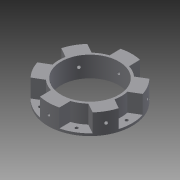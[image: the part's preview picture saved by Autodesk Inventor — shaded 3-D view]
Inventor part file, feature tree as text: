
AUTODESK INVENTOR PART (.ipt)
format: ipt  version: 2015 (Build 190159000, 159)  size: 173,056 bytes
history: native  units: in
note: dims shown in document units (in); Inventor stores cm internally (conversion verified against a paired STEP export)
features: sketch x5, extrude x3, hole x2, pattern_circular x2, plane x1
ambient origin geometry x8: Origin, YZ Plane, XZ Plane, XY Plane, X Axis, Y Axis, Z Axis, Center Point
bodies: Solid1 (feature_tree)
feature tree (13):
  extrude  "Extrusion1"  Depth=7.0in
  extrude  "Extrusion2"  Depth=5.21in
  hole  "Hole1"  [1 undecoded]
  pattern_circular  "Circular Pattern1"  [2 undecoded]
  extrude  "Extrusion3"  Depth=0.3225in
  plane  "Work Plane3"
  hole  "Hole3"  [1 undecoded]
  pattern_circular  "Circular Pattern3"  [2 undecoded]
  sketch  "Sketch1"  dims[d0=4.81in d1=7.0in]
  sketch  "Sketch2"  dims[d2=0.2in d3=0.0in d4=5.21in]
  sketch  "Sketch3"  dims[d5=4.81in d6=1.51in d7=0.0in]
  sketch  "Sketch4"  dims[d8=0.895in]
  sketch  "Sketch6"  dims[d9=0.4475in d10=0.25in d11=0.3225in d12=0.25in d13=0.75in d14=0.375in d15=0.25in d16=0.5635in d17=1.0in d18=0.8108in d19=2.3622in d20=360.0deg d22=1.51in d23=0.0in d35=0.855in d36=0.25in d37=0.25in d38=0.75in d39=0.375in d40=0.25in d41=0.5635in d42=1.5425in d43=0.8108in d44=2.3622in d45=360.0deg]
note: 6 required parameter values undecoded (feature->parameter linkage not recoverable at this tier; creation-order binding heuristic only, values carry confidence <= 0.55)
